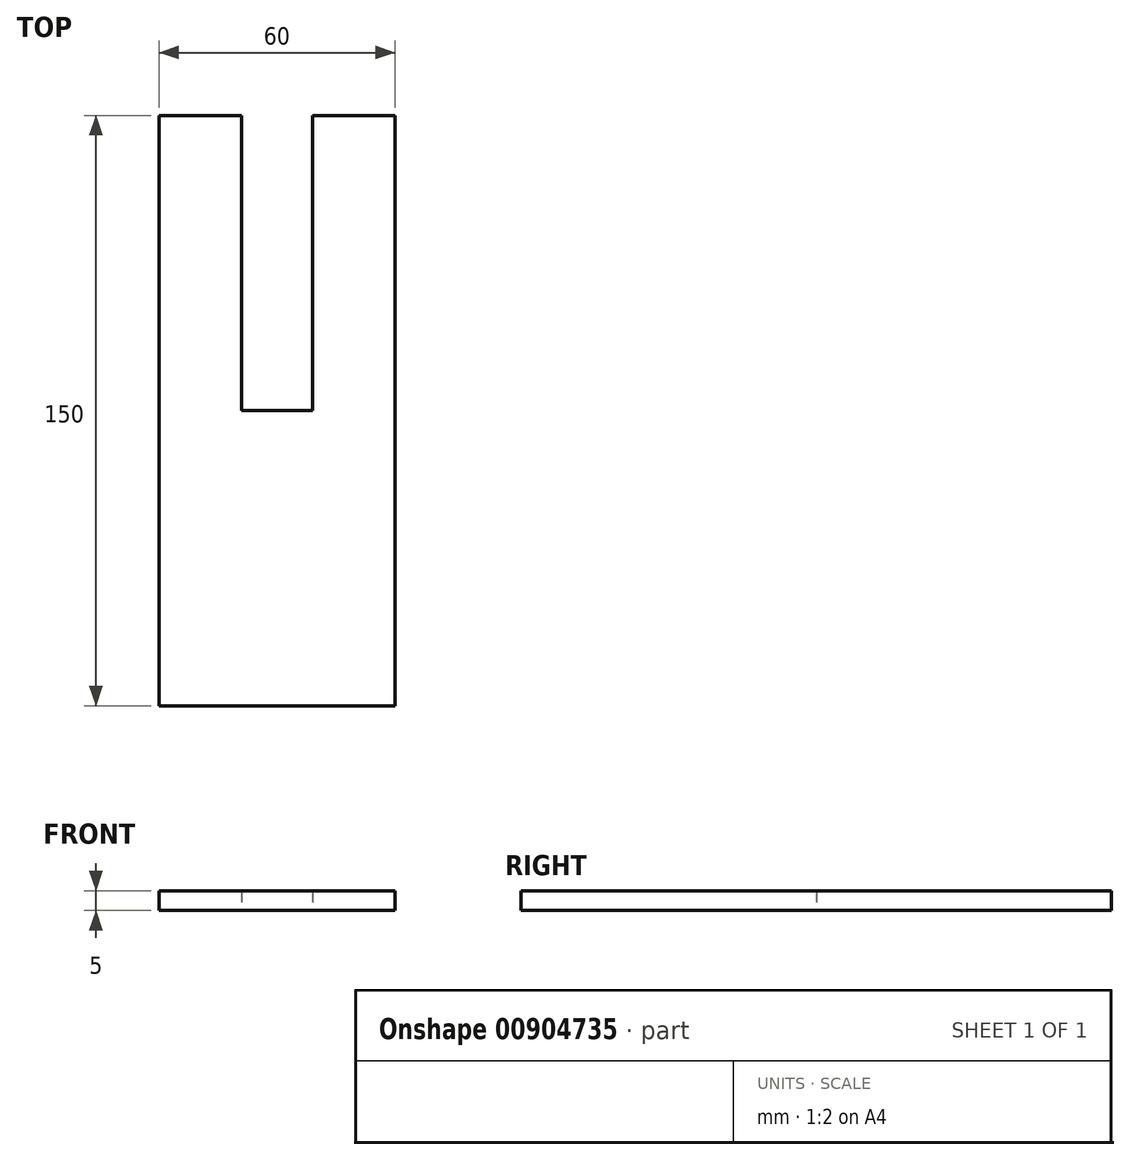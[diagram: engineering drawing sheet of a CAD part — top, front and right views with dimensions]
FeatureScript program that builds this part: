
annotation { "Feature Type Name" : "Feature", "Feature Type Description" : "" }
export const myFeature = defineFeature(function(context is Context, id is Id, definition is map)
    precondition{}
    {
        {
            var Q0;
            Q0=qCreatedBy(makeId("Top.planeOp"),FACE);
            var sketch = newSketch(context, id + "F0", { "sketchPlane" : qUnion([Q0])});
            skLineSegment(sketch, "E0", {"start": v(0, 0) * mm, "end": v(0, 150) * mm, "construction": true});
            skLineSegment(sketch, "E1", {"start": v(0, 150) * mm, "end": v(-9, 150) * mm, "construction": true});
            skLineSegment(sketch, "E2", {"start": v(-9, 150) * mm, "end": v(-30, 150) * mm});
            skLineSegment(sketch, "E3", {"start": v(-30, 150) * mm, "end": v(-30, 0) * mm});
            skLineSegment(sketch, "E4", {"start": v(-30, 0) * mm, "end": v(0, 0) * mm});
            skLineSegment(sketch, "E5", {"start": v(-9, 150) * mm, "end": v(-9, 75) * mm});
            skLineSegment(sketch, "E6", {"start": v(-9, 75) * mm, "end": v(0, 75) * mm});
            skLineSegment(sketch, "E7.MirrorCS", {"start": v(9, 75) * mm, "end": v(0, 75) * mm});
            skLineSegment(sketch, "E8.MirrorCS", {"start": v(9, 150) * mm, "end": v(9, 75) * mm});
            skLineSegment(sketch, "E9.MirrorCS", {"start": v(9, 150) * mm, "end": v(30, 150) * mm});
            skLineSegment(sketch, "E10.MirrorCS", {"start": v(30, 150) * mm, "end": v(30, 0) * mm});
            skLineSegment(sketch, "E11.MirrorCS", {"start": v(30, 0) * mm, "end": v(0, 0) * mm});
            skSolve(sketch);
        }
        {
            var Q0;
            Q0=qSketchRegion(id+"F0",true);
            extrude(context, id + "F1", {"entities" : qUnion([Q0]), "depth" : 5 * mm, "offsetDistance" : 25 * mm});
        }
    });
